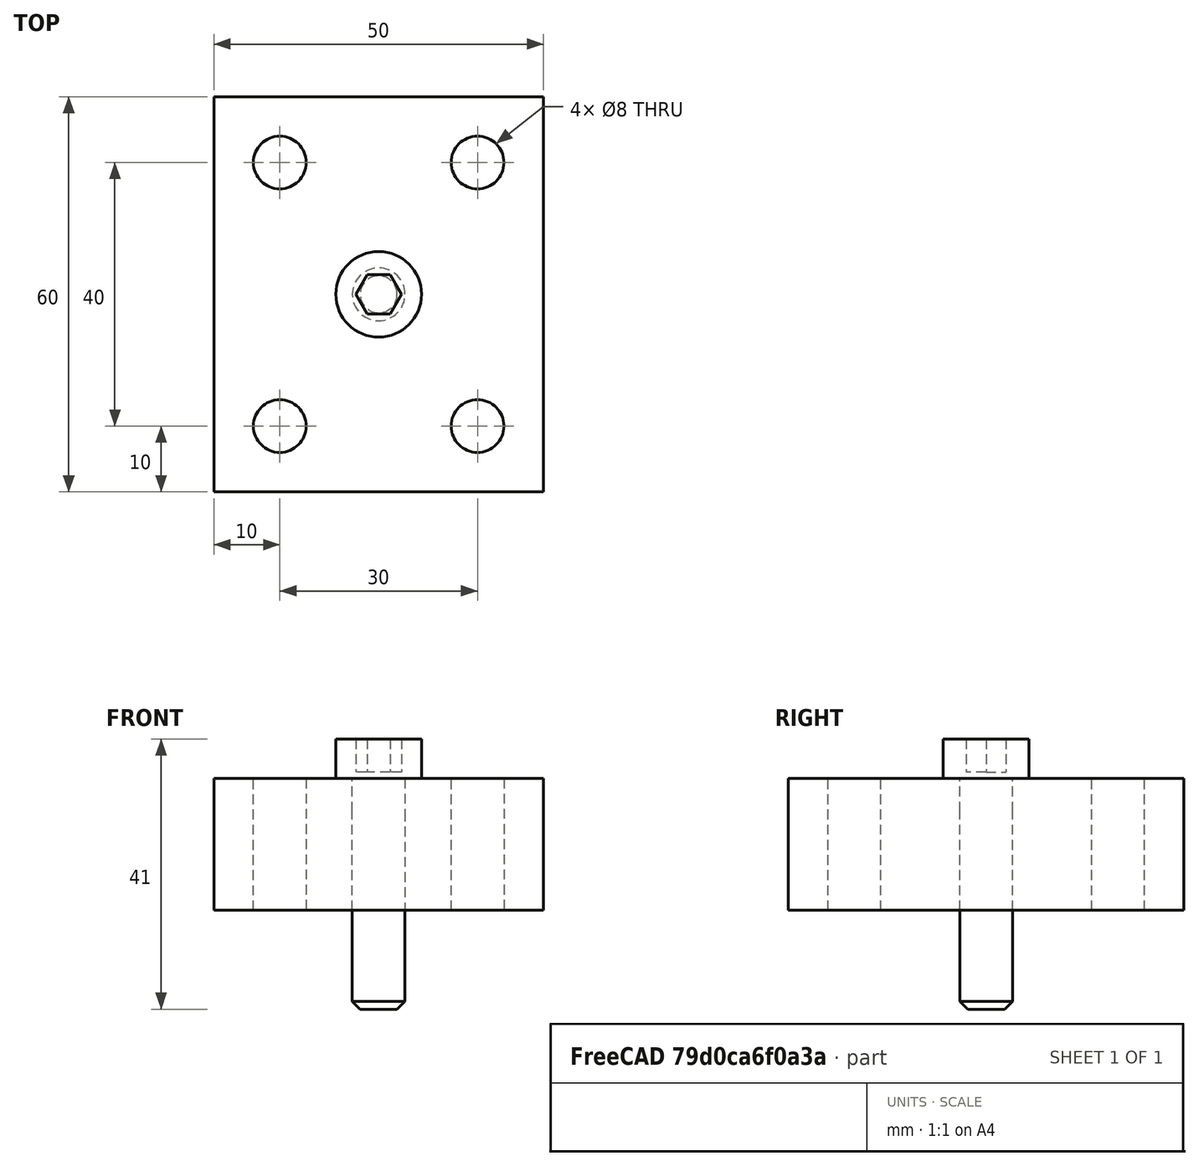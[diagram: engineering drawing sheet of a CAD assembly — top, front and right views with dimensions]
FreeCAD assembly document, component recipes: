
FREECAD ASSEMBLY — COMPONENT RECIPES ("xrepo")

This assembly document has 2 components, labeled P0..P1 below (a component is one placed body or linked part). 2 of them carry a construction recipe — the FreeCAD feature program that regenerates the part from scratch, quoted from this document or its linked companion documents; the rest are supplied as boundary geometry only. No exploded tour is included for this assembly.
COMPONENT P0 — recipe-attached ("Body002", modeled in this document).
Construction recipe (the document's own serialized feature program — sketch geometry with constraints, then the solid features built on it; lengths are millimeters unless a unit is written):

FEATURE [Sketcher::SketchObject] Sketch002
  MapMode = 5
  Support = -> [XY_Plane002]
  sketch-geometry (1):
    g0: Circle CenterX=0 CenterY=0 CenterZ=0 NormalX=0 NormalY=0 NormalZ=1 AngleXU=0 Radius=4
  constraints (2):
    c: Coincident(g0,g-1)
    c: Diameter(g0) = 8  'D1'
FEATURE [PartDesign::Pad] Pad002
  ClaimChildren = false
  Length = 5
  Length2 = 100
  Profile = -> Sketch002
  Reversed = true
  Type = 0
FEATURE [Sketcher::SketchObject] Sketch003
  ExternalGeometry = -> [Pad002]
  MapMode = 5
  Placement = pos=(0,0,-5) rot=(1,0,0;3.14159rad)
  Support = -> [Pad002]
FEATURE [PartDesign::Pad] Pad003
  BaseFeature = -> Pad002
  ClaimChildren = false
  Length = 30
  Length2 = 100
  Profile = -> Sketch003
  Type = 0
  expr: Length = Pad005.Length + 10mm
FEATURE [Sketcher::SketchObject] Sketch004
  MapMode = 5
  Support = -> [XY_Plane002]
  sketch-geometry (1):
    g0: Circle CenterX=0 CenterY=0 CenterZ=0 NormalX=0 NormalY=0 NormalZ=1 AngleXU=0 Radius=6.5
  constraints (2):
    c: Coincident(g0,g-1)
    c: Diameter(g0) = 13  'DH'
FEATURE [PartDesign::Pad] Pad004
  BaseFeature = -> Pad003
  ClaimChildren = false
  Length = 6
  Length2 = 100
  Profile = -> Sketch004
  Type = 0
FEATURE [Sketcher::SketchObject] Sketch005
  MapMode = 5
  Placement = pos=(0,0,6) rot=(0,0,1;0rad)
  Support = -> [Pad004]
  sketch-geometry (7):
    g0: LineSegment StartX=3.4641 StartY=0 StartZ=0 EndX=1.73205 EndY=3 EndZ=0
    g1: LineSegment StartX=1.73205 StartY=3 StartZ=0 EndX=-1.73205 EndY=3 EndZ=0
    g2: LineSegment StartX=-1.73205 StartY=3 StartZ=0 EndX=-3.4641 EndY=0 EndZ=0
    g3: LineSegment StartX=-3.4641 StartY=0 StartZ=0 EndX=-1.73205 EndY=-3 EndZ=0
    g4: LineSegment StartX=-1.73205 StartY=-3 StartZ=0 EndX=1.73205 EndY=-3 EndZ=0
    g5: LineSegment StartX=1.73205 StartY=-3 StartZ=0 EndX=3.4641 EndY=0 EndZ=0
    g6: Circle [constr] CenterX=0 CenterY=0 CenterZ=0 NormalX=0 NormalY=0 NormalZ=1 AngleXU=0 Radius=3.4641
  constraints (16):
    c: Coincident(g0,g1)
    c: Coincident(g1,g2)
    c: Coincident(g2,g3)
    c: Coincident(g3,g4)
    c: Coincident(g4,g5)
    c: Coincident(g5,g0)
    c: Equal(g0, g1-g5) x5
    c: PointOnObject(g0,g6)
    c: PointOnObject(g1,g6)
    c: PointOnObject(g2,g6)
    c: PointOnObject(g3,g6)
    c: PointOnObject(g4,g6)
    c: PointOnObject(g5,g6)
    c: Coincident(g6,g-1)
    c: PointOnObject(g5,g-1)
    c: Distance(g0,g4) = 6  'WS'
FEATURE [PartDesign::Pocket] Pocket
  BaseFeature = -> Pad004
  ClaimChildren = false
  Length = 5
  Length2 = 100
  Profile = -> Sketch005
  Type = 0
FEATURE [PartDesign::Chamfer] Chamfer
  Base = -> Pocket [Edge6]
  BaseFeature = -> Pocket
  Size = 1.2
FEATURE [PartDesign::Body] Body002
  Group = -> [Sketch002,Pad002,Sketch003,Pad003,Sketch004,Pad004,Sketch005,Pocket,Chamfer]
  Origin = -> Origin002
  Tip = -> Chamfer
COMPONENT P1 — recipe-attached ("Body003", modeled in this document).
Construction recipe (the document's own serialized feature program — sketch geometry with constraints, then the solid features built on it; lengths are millimeters unless a unit is written):

FEATURE [Sketcher::SketchObject] Sketch006
  MapMode = 5
  Support = -> [XY_Plane003]
  sketch-geometry (8):
    g0: Circle CenterX=-15 CenterY=20 CenterZ=0 NormalX=0 NormalY=0 NormalZ=1 AngleXU=0 Radius=4
    g1: Circle CenterX=15 CenterY=20 CenterZ=0 NormalX=0 NormalY=0 NormalZ=1 AngleXU=0 Radius=4
    g2: Circle CenterX=15 CenterY=-20 CenterZ=0 NormalX=0 NormalY=0 NormalZ=1 AngleXU=0 Radius=4
    g3: Circle CenterX=-15 CenterY=-20 CenterZ=0 NormalX=0 NormalY=0 NormalZ=1 AngleXU=0 Radius=4
    g4: LineSegment StartX=-25 StartY=30 StartZ=0 EndX=25 EndY=30 EndZ=0
    g5: LineSegment StartX=25 StartY=30 StartZ=0 EndX=25 EndY=-30 EndZ=0
    g6: LineSegment StartX=25 StartY=-30 StartZ=0 EndX=-25 EndY=-30 EndZ=0
    g7: LineSegment StartX=-25 StartY=-30 StartZ=0 EndX=-25 EndY=30 EndZ=0
  constraints (19):
    c: Equal(g0,g1)
    c: Equal(g1,g2)
    c: Equal(g2,g3)
    c: Diameter(g0) = 8  'BHD'
    c: Symmetric(g0,g1,g-2)
    c: Symmetric(g1,g2,g-1)
    c: Symmetric(g0,g3,g-1)
    c: Coincident(g4,g5)
    c: Coincident(g5,g6)
    c: Coincident(g6,g7)
    c: Coincident(g7,g4)
    c: Horizontal(g6)
    c: Vertical(g7)
    c: Symmetric(g4,g4,g-2)
    c: Symmetric(g4,g5,g-1)
    c: Distance(g3,g2) = 30  'L1'
    c: Distance(g4) = 50  'L2'
    c: Distance(g1,g2) = 40  'W1'
    c: Distance(g7) = 60  'W2'
FEATURE [PartDesign::Pad] Pad005
  ClaimChildren = false
  Length = 20
  Length2 = 100
  Profile = -> Sketch006
  Reversed = true
  Type = 0
FEATURE [PartDesign::Body] Body003
  Group = -> [Sketch006,Pad005]
  Origin = -> Origin003
  Tip = -> Pad005
PROVENANCE & LICENSES
A FreeCAD (.FCStd) document from a public repository crawl; recipes are the document's own serialized feature recipes (and, for linked parts, companion documents' recipes).
License: as declared in the source repository (recorded in the dataset sidecar).
